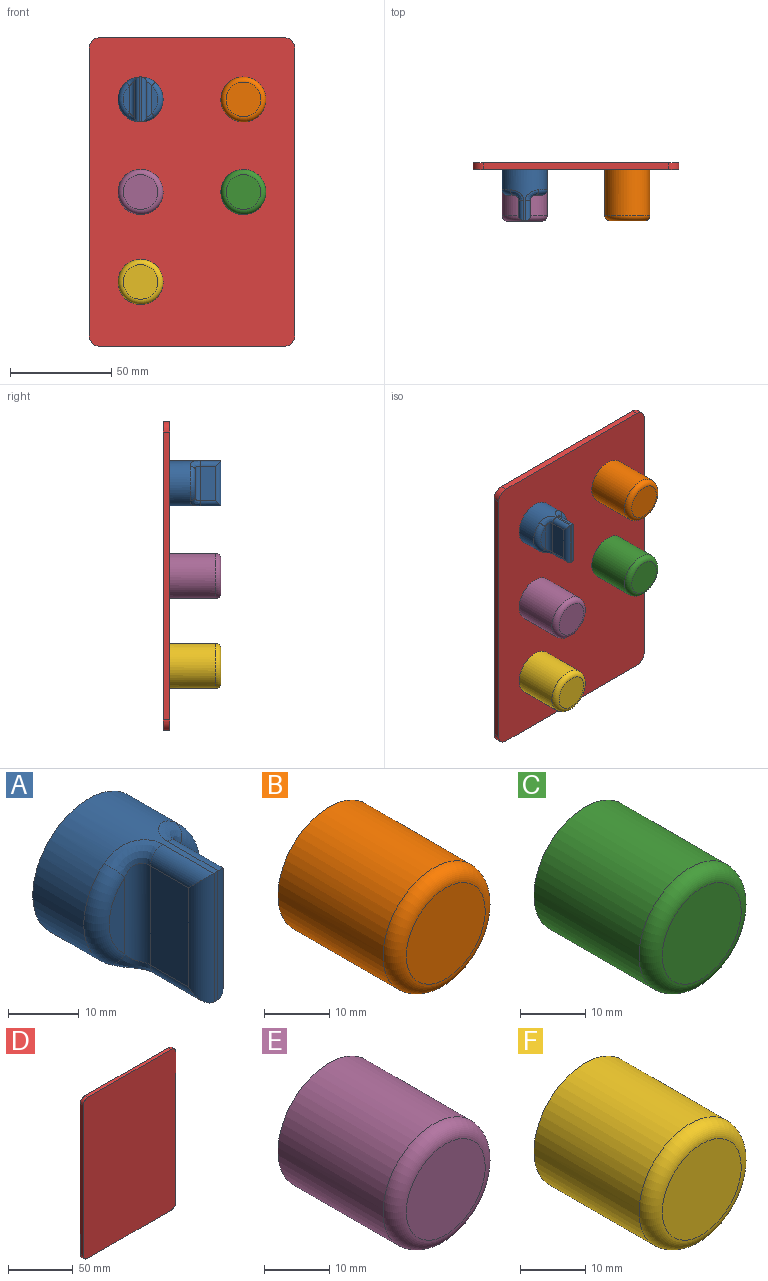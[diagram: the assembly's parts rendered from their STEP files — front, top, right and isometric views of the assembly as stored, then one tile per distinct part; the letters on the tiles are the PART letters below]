
ASSEMBLY  parts=6 mates=5
PART A: 21 faces, bbox 24.1x25.4x22.2 mm
  f0: plane 22.23x0.74mm, normal (0,-1,0), area 16.3mm2, adj f1,f12,f19
  f1: cylinder r=11.11mm len=25.4mm, axis (0,1,0), area 767.8mm2, adj f0,f2,f7,f9,f10,f11,f12,f13
  f2: plane 22.23x22.23mm, normal (0,1,0), area 387.9mm2, adj f1
  f3: plane 17.13x7.62mm, normal (1,0,0), area 130.5mm2, adj f8,f10,f12,f13
  f4: plane 13.24x3.13mm, normal (0,-1,0), area 28.8mm2, adj f8,f9
  f5: plane 17.13x7.62mm, normal (-1,0,0), area 130.5mm2, adj f15,f17,f19,f20
  f6: plane 13.24x3.13mm, normal (0,-1,0), area 28.8mm2, adj f15,f16
  f7: bspline ~7.84x6.22mm, area 25.6mm2, adj f1,f8,f9,f10
  f8: cylinder r=2.54mm len=17.13mm, axis (0,0,-1), area 64.8mm2, adj f3,f4,f7,f11
  f9: torus R=8.57mm, axis (0,-1,0), area 71.7mm2, adj f1,f4,f7,f11
  f10: cylinder r=2.54mm len=10.16mm, axis (0,1,0), area 35.7mm2, adj f1,f3,f7,f12
  f11: bspline ~8.17x6.14mm, area 25.6mm2, adj f1,f8,f9,f13
  f12: cylinder r=2.54mm len=22.21mm, axis (0,0,1), area 81.2mm2, adj f0,f1,f3,f10,f13
  f13: cylinder r=2.54mm len=10.16mm, axis (0,1,0), area 35.7mm2, adj f1,f3,f11,f12
  f14: bspline ~7.84x6.22mm, area 25.6mm2, adj f1,f15,f16,f17
  f15: cylinder r=2.54mm len=17.13mm, axis (0,0,1), area 64.8mm2, adj f5,f6,f14,f18
  f16: torus R=8.57mm, axis (0,-1,0), area 71.7mm2, adj f1,f6,f14,f18
  f17: cylinder r=2.54mm len=10.16mm, axis (0,1,0), area 35.7mm2, adj f1,f5,f14,f19
  f18: bspline ~8.17x6.14mm, area 25.6mm2, adj f1,f15,f16,f20
  f19: cylinder r=2.54mm len=22.21mm, axis (0,0,-1), area 81.2mm2, adj f0,f1,f5,f17,f20
  f20: cylinder r=2.54mm len=10.16mm, axis (0,1,0), area 35.7mm2, adj f1,f5,f18,f19
PART B: 4 faces, bbox 24.1x25.4x24.1 mm
  f0: cylinder r=11.11mm len=22.86mm, axis (0,1,0), area 1596.1mm2, adj f2,f3
  f1: plane 17.15x17.15mm, normal (0,-1,0), area 230.9mm2, adj f3
  f2: plane 22.23x22.23mm, normal (0,1,0), area 387.9mm2, adj f0
  f3: torus R=8.57mm, axis (0,-1,0), area 255.4mm2, adj f0,f1
PART C: 4 faces, bbox 24.1x25.4x24.1 mm
  f0: cylinder r=11.11mm len=22.86mm, axis (0,1,0), area 1596.1mm2, adj f2,f3
  f1: plane 17.15x17.15mm, normal (0,-1,0), area 230.9mm2, adj f3
  f2: plane 22.23x22.23mm, normal (0,1,0), area 387.9mm2, adj f0
  f3: torus R=8.57mm, axis (0,-1,0), area 255.4mm2, adj f0,f1
PART D: 10 faces, bbox 101.6x3.2x152.4 mm
  f0: plane 91.44x3.18mm, normal (0,0,-1), area 290.3mm2, adj f4,f5,f6,f9
  f1: plane 142.24x3.18mm, normal (1,0,0), area 451.6mm2, adj f4,f5,f6,f7
  f2: plane 91.44x3.18mm, normal (0,0,1), area 290.3mm2, adj f4,f5,f7,f8
  f3: plane 142.24x3.18mm, normal (-1,0,0), area 451.6mm2, adj f4,f5,f8,f9
  f4: plane 152.4x101.6mm, normal (0,1,0), area 15461.7mm2, adj f0,f1,f2,f3,f6,f7,f8,f9
  f5: plane 152.4x101.6mm, normal (0,-1,0), area 15461.7mm2, adj f0,f1,f2,f3,f6,f7,f8,f9
  f6: cylinder r=5.08mm len=5.08mm, axis (0,-1,0), area 25.3mm2, adj f0,f1,f4,f5
  f7: cylinder r=5.08mm len=5.08mm, axis (0,1,0), area 25.3mm2, adj f1,f2,f4,f5
  f8: cylinder r=5.08mm len=5.08mm, axis (0,-1,0), area 25.3mm2, adj f2,f3,f4,f5
  f9: cylinder r=5.08mm len=5.08mm, axis (0,1,0), area 25.3mm2, adj f0,f3,f4,f5
PART E: 4 faces, bbox 24.1x25.4x24.1 mm
  f0: cylinder r=11.11mm len=22.86mm, axis (0,1,0), area 1596.1mm2, adj f2,f3
  f1: plane 17.15x17.15mm, normal (0,-1,0), area 230.9mm2, adj f3
  f2: plane 22.23x22.23mm, normal (0,1,0), area 387.9mm2, adj f0
  f3: torus R=8.57mm, axis (0,-1,0), area 255.4mm2, adj f0,f1
PART F: 4 faces, bbox 24.1x25.4x24.1 mm
  f0: cylinder r=11.11mm len=22.86mm, axis (0,1,0), area 1596.1mm2, adj f2,f3
  f1: plane 17.15x17.15mm, normal (0,-1,0), area 230.9mm2, adj f3
  f2: plane 22.23x22.23mm, normal (0,1,0), area 387.9mm2, adj f0
  f3: torus R=8.57mm, axis (0,-1,0), area 255.4mm2, adj f0,f1
PLACE A t=(-1020.72,93.8,1101.09)mm
PLACE B t=(-1020.72,93.8,1101.09)mm
PLACE C t=(-1020.72,93.8,1106.17)mm
PLACE D t=(-1020.72,93.8,1106.16)mm
PLACE E t=(-1020.72,93.8,1106.17)mm
PLACE F t=(-1020.72,93.8,1112.52)mm
MATE fastened B.f0 <-> D.f5  axis (0,1,0) through (-969.92,93.8,1151.89)mm
MATE fastened F.f0 <-> D.f5  axis (0,1,0) through (-1020.72,93.8,1061.72)mm
MATE fastened A.f1 <-> D.f5  axis (0,1,0) through (-1020.72,93.8,1151.89)mm
MATE fastened C.f0 <-> D.f5  axis (0,1,0) through (-969.92,93.8,1106.17)mm
MATE fastened E.f0 <-> D.f5  axis (0,1,0) through (-1020.72,93.8,1106.17)mm
